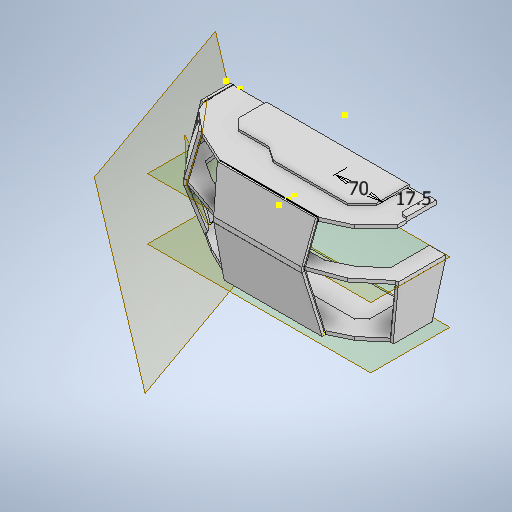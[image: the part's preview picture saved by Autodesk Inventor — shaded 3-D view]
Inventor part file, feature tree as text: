
AUTODESK INVENTOR PART (.ipt)
format: ipt  version: 2025.2 (Build 292293000, 293)  size: 5,318,656 bytes
history: native  units: mm
features: sketch x29, extrude x21, other x15, loft x7, plane x5
ambient origin geometry x8: Origin, YZ Plane, XZ Plane, XY Plane, X Axis, Y Axis, Z Axis, Center Point
bodies: Body1 (feature_tree)
feature tree (77):
  extrude  "Extrusion2"  Depth=45.0mm
  extrude  "Extrusion3"  Depth=40.0mm
  plane  "Work Plane3"
  extrude  "Extrusion4"  Depth=145.0mm
  extrude  "Extrusion5"  Depth=55.0mm
  plane  "Work Plane4"
  extrude  "Extrusion6"  Depth=40.0mm
  sketch  "Sketch8"  dims[d17=165.0deg d18=15.0mm]
  sketch  "Sketch9"  dims[d20=10.0mm d21=40.0mm]
  sketch  "Sketch10"  dims[d22=5.0mm d23=5.0mm]
  loft  "Loft1"
  loft  "Loft2"
  extrude  "Extrusion7"  Depth=5.0mm
  extrude  "Extrusion8"  TaperAngle=90.0deg  [1 undecoded]
  extrude  "Extrusion9"  Depth=30.0mm
  sketch  "Sketch14"  dims[d30=45.0mm d31=20.0mm]
  sketch  "Sketch15"  dims[d32=45.0deg d39=5.0mm d40=0.0mm]
  sketch  "Sketch16"  dims[d41=3.0mm d42=3.0mm d43=0.0mm d44=0.0mm d45=150.0mm]
  loft  "Loft3"
  loft  "Loft4"
  loft  "Loft5"
  extrude  "Extrusion10"  Depth=150.0mm
  extrude  "Extrusion11"  Depth=10.0mm
  extrude  "Extrusion12"  Depth=10.0mm
  extrude  "Extrusion13"  Depth=10.0mm
  extrude  "Extrusion14"  Depth=10.0mm
  loft  "Loft7"
  loft  "Loft8"
  sketch  "Sketch22"  dims[d57=10.0mm d58=10.0mm]
  plane  "Work Plane5"
  extrude  "Extrusion15"  Depth=3.0mm TaperAngle=0.0deg
  plane  "Work Plane6"
  extrude  "Extrusion16"  Depth=10.0mm
  extrude  "Extrusion17"  Depth=50.0mm
  plane  "Work Plane7"
  extrude  "Extrusion18"  Depth=50.0mm
  sketch  "Sketch28"  dims[d71=27.925268mm d72=10.0mm]
  extrude  "Extrusion19"  Depth=10.0mm
  extrude  "Extrusion20"  Depth=60.0mm
  extrude  "Extrusion21"  Depth=5.0mm TaperAngle=0.0deg
  extrude  "Extrusion22"  TaperAngle=0.0deg  [1 undecoded]
  sketch  "Sketch1"  dims[d6=115.0mm d8=45.0mm]
  other  "Image1"
  sketch  "Sketch3"  dims[d9=45.0deg d10=40.0mm]
  sketch  "Sketch4"  dims[d11=27.925268mm d12=145.0mm]
  sketch  "Sketch5"  dims[d13=27.052603mm d14=55.0mm]
  sketch  "Sketch6"  dims[d15=27.052603mm d16=40.0mm]
  other  "Edges1"
  other  "Edges2"
  other  "Edges3"
  other  "Edges4"
  sketch  "Sketch11"  dims[d24=40.0mm d25=90.0deg]
  sketch  "Sketch12"  dims[d26=30.0mm d27=110.0mm]
  sketch  "Sketch13"  dims[d28=25.0mm d29=25.307274mm]
  other  "Edges5"
  other  "Edges6"
  other  "Edges7"
  other  "Edges8"
  other  "Edges9"
  other  "Edges10"
  sketch  "Sketch17"  dims[d46=10.0mm d48=10.0mm]
  sketch  "Sketch18"  dims[d49=10.0mm d50=22.68928mm]
  sketch  "Sketch19"  dims[d51=10.0mm d52=10.0mm]
  sketch  "Sketch20"  dims[d53=10.0mm d54=10.0mm]
  sketch  "Sketch21"  dims[d55=10.0mm d56=10.0mm]
  other  "Edges13"
  other  "Edges14"
  other  "Edges15"
  other  "Edges16"
  sketch  "Sketch23"  dims[d59=5.0mm d60=0.0mm d61=3.0mm d62=3.0mm d63=0.0mm d64=0.0mm]
  sketch  "Sketch24"  dims[d65=-90.0mm d66=10.0mm]
  sketch  "Sketch25"  dims[d67=70.0mm d68=50.0mm]
  sketch  "Sketch26"  dims[d69=22.68928mm d70=50.0mm]
  sketch  "Sketch29"  dims[d73=50.0mm d74=60.0mm]
  sketch  "Sketch30"  dims[d75=70.0mm d76=5.0mm d77=0.0mm]
  sketch  "Sketch31"  dims[d78=0.0mm d79=90.0deg d80=0.0mm d81=90.0deg]
  sketch  "Sketch32"  dims[d82=0.0mm d83=90.0deg d84=0.0mm d85=90.0deg d86=4.0mm d87=0.0mm d88=4.0mm d89=0.0mm d90=4.0mm d91=0.0mm d92=0.0mm d93=90.0deg d94=0.0mm d95=90.0deg d96=0.0mm d97=90.0deg d98=0.0mm d99=90.0deg d100=0.0mm d101=90.0deg d102=0.0mm d103=90.0deg d104=4.0mm d105=0.0mm d106=4.0mm d107=0.0mm d108=4.0mm d109=0.0mm d110=4.0mm d111=0.0mm d112=4.0mm d113=0.0mm d118=0.0mm d119=90.0deg d120=0.0mm d121=90.0deg d122=0.0mm d123=90.0deg d124=0.0mm d125=90.0deg d126=4.0mm d127=0.0mm d128=4.0mm d129=0.0mm d130=4.0mm d131=0.0mm d132=92.689mm d133=4.0mm d134=0.0mm d135=70.0mm d136=17.5mm d137=5.0mm d138=25.0mm d139=70.0mm d140=25.0mm d141=17.5mm d142=90.0deg d143=23.0mm d144=0.0mm d145=70.0mm d146=3.0mm d147=17.5mm d148=0.0mm d149=25.0mm d150=30.0mm d151=15.0deg d152=90.0deg d153=5.0mm d154=20.0mm d155=90.0deg d156=4.363323mm d157=17.5mm d158=0.0mm d159=25.0mm d160=165.0deg d161=40.0mm d162=150.0deg d163=50.0mm d164=1.745329mm d165=40.0mm d166=5.0mm d167=40.0mm d168=30.543262mm d169=17.5mm d170=0.0mm]
note: 2 required parameter values undecoded (feature->parameter linkage not recoverable at this tier; creation-order binding heuristic only, values carry confidence <= 0.55)
